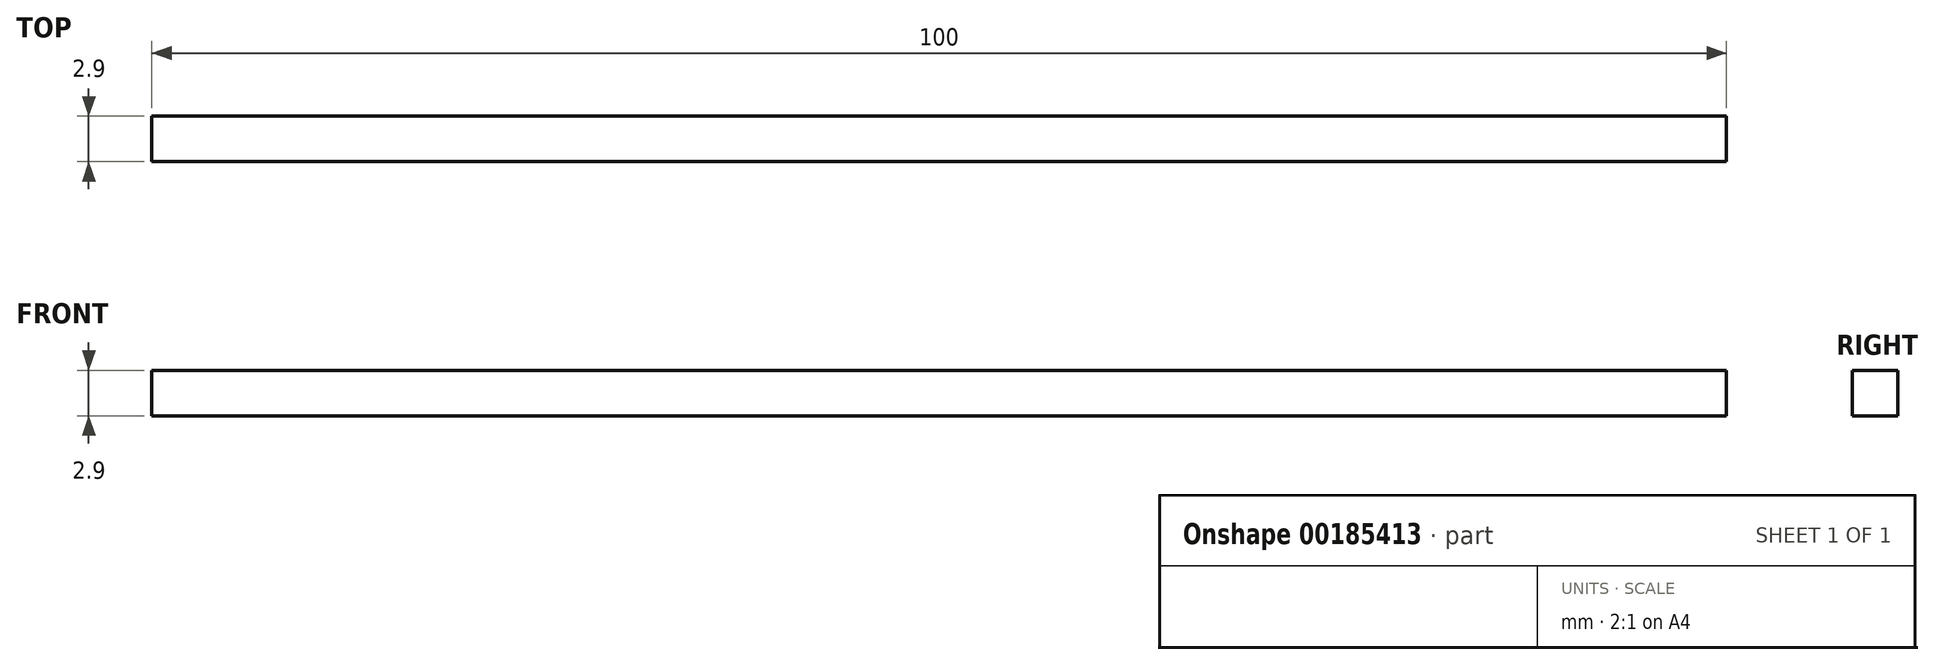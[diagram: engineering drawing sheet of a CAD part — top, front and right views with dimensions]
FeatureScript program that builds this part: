
annotation { "Feature Type Name" : "Feature", "Feature Type Description" : "" }
export const myFeature = defineFeature(function(context is Context, id is Id, definition is map)
    precondition{}
    {
        {
            var Q0;
            Q0=qCreatedBy(makeId("Front.planeOp"),FACE);
            var sketch = newSketch(context, id + "F0", { "sketchPlane" : qUnion([Q0])});
            skLineSegment(sketch, "E0.bottom", {"start": v(-50, 1.45) * mm, "end": v(50, 1.45) * mm});
            skLineSegment(sketch, "E0.top", {"start": v(-50, -1.45) * mm, "end": v(50, -1.45) * mm});
            skLineSegment(sketch, "E0.left", {"start": v(-50, 1.45) * mm, "end": v(-50, -1.45) * mm});
            skLineSegment(sketch, "E0.right", {"start": v(50, 1.45) * mm, "end": v(50, -1.45) * mm});
            skPoint(sketch, "E0.middle", {"position": v(0, 0) * mm});
            skSolve(sketch);
        }
        {
            var Q0;
            Q0=makeQuery(id+"F0.imprint","IMPRINT",FACE,{"disambiguationData":[TD([[makeQuery(id+"F0.imprint","IMPRINT",EDGE,{"derivedFrom":sQuery(id+"F0.wireOp",EDGE,"E0.bottom")}),-1.0]])]});
            extrude(context, id + "F1", {"entities" : qUnion([Q0]), "endBound" : BoundingType.SYMMETRIC, "depth" : 2.9 * mm});
        }
    });
